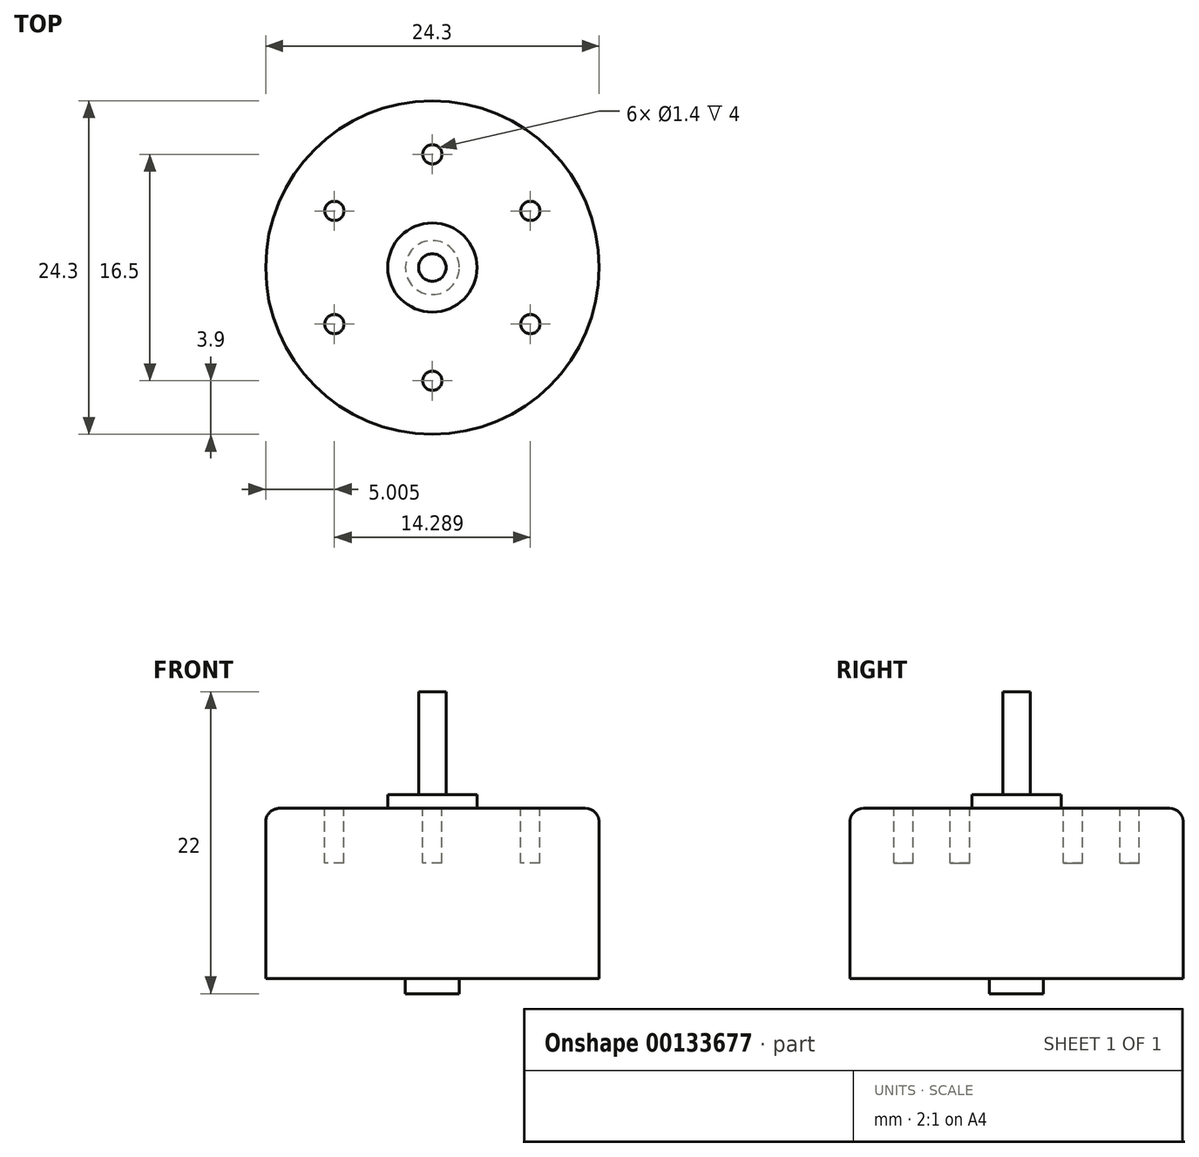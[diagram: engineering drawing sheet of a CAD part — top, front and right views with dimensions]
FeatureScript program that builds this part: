
annotation { "Feature Type Name" : "Feature", "Feature Type Description" : "" }
export const myFeature = defineFeature(function(context is Context, id is Id, definition is map)
    precondition{}
    {
        {
            var Q0;
            Q0=qCreatedBy(makeId("Front.planeOp"),FACE);
            var sketch = newSketch(context, id + "F0", { "sketchPlane" : qUnion([Q0])});
            skLineSegment(sketch, "E0", {"start": v(0, 0) * mm, "end": v(0, 20.9) * mm});
            skLineSegment(sketch, "E1", {"start": v(0, 20.9) * mm, "end": v(-1, 20.9) * mm});
            skLineSegment(sketch, "E2", {"start": v(-1, 20.9) * mm, "end": v(-1, 13.4) * mm});
            skLineSegment(sketch, "E3", {"start": v(-1, 13.4) * mm, "end": v(-3.25, 13.4) * mm});
            skLineSegment(sketch, "E4", {"start": v(-3.25, 13.4) * mm, "end": v(-3.25, 12.4) * mm});
            skLineSegment(sketch, "E5", {"start": v(-3.25, 12.4) * mm, "end": v(-12.15, 12.4) * mm});
            skLineSegment(sketch, "E6", {"start": v(-12.15, 12.4) * mm, "end": v(-12.15, 0) * mm});
            skLineSegment(sketch, "E7", {"start": v(-12.15, 0) * mm, "end": v(-1.97, 0) * mm});
            skLineSegment(sketch, "E8", {"start": v(-1.97, 0) * mm, "end": v(-1.97, -1.1) * mm});
            skLineSegment(sketch, "E9", {"start": v(-1.97, -1.1) * mm, "end": v(0, -1.1) * mm});
            skLineSegment(sketch, "E10", {"start": v(0, -1.1) * mm, "end": v(0, 0) * mm});
            skSolve(sketch);
        }
        {
            var Q0;
            Q0=makeQuery(id+"F0.imprint","IMPRINT",FACE,{"disambiguationData":[TD([[makeQuery(id+"F0.imprint","IMPRINT",EDGE,{"derivedFrom":sQuery(id+"F0.wireOp",EDGE,"E0")}),1.0]])]});
            var Q1;
            Q1=sQuery(id+"F0.wireOp",EDGE,"E0");
            revolve(context, id + "F1", {"entities" : qUnion([Q0]), "axis" : qUnion([Q1]), "revolveType" : RevolveType.FULL});
        }
        {
            var Q0;
            Q0=makeQuery(id+"F1.opRevolve","SWEPT_FACE",FACE,{"disambiguationData":[OSD([sQuery(id+"F0.wireOp",EDGE,"E5")])]});
            var sketch = newSketch(context, id + "F2", { "sketchPlane" : qUnion([Q0])});
            skLineSegment(sketch, "E11", {"start": v(0, 0) * mm, "end": v(0, 8.25) * mm});
            skCircle(sketch, "E12", {"center": v(0, 8.25) * mm, "radius": 0.7 * mm});
            skCircle(sketch, "E13.1.0", {"center": v(-7.14, 4.13) * mm, "radius": 0.7 * mm});
            skCircle(sketch, "E13.2.0", {"center": v(-7.14, -4.12) * mm, "radius": 0.7 * mm});
            skCircle(sketch, "E13.3.0", {"center": v(0, -8.25) * mm, "radius": 0.7 * mm});
            skCircle(sketch, "E13.4.0", {"center": v(7.14, -4.13) * mm, "radius": 0.7 * mm});
            skCircle(sketch, "E13.5.0", {"center": v(7.14, 4.13) * mm, "radius": 0.7 * mm});
            skPoint(sketch, "E13.center", {"position": v(0, 0) * mm});
            skSolve(sketch);
        }
        {
            var Q0;
            Q0=qSketchRegion(id+"F2",true);
            extrude(context, id + "F3", {"entities" : qUnion([Q0]), "operationType" : NewBodyOperationType.REMOVE, "oppositeDirection" : true, "depth" : 4 * mm});
        }
        {
            var Q0;
            Q0=makeQuery(id+"F1.opRevolve","SWEPT_EDGE",EDGE,{"disambiguationData":[OSD([sQuery(id+"F0.wireOp",EDGE,"E5"),sQuery(id+"F0.wireOp",EDGE,"E6")])]});
            fillet(context, id + "F4", {"entities" : qUnion([Q0]), "radius" : 1 * mm, "tangentPropagation" : true, "allowEdgeOverflow" : false});
        }
    });
